# Revit family: Sink-Undermount-Kitchen-KOHLER-Tight-K-33710_1
name_source: partatom
category: Plumbing Fixtures
units: mm (PartAtom-declared; Revit-internal decimal feet)

## family parameters
Cut with Voids When Loaded = No
Host = Face
OmniClass Number = 23.31.13.00
OmniClass Title = Sinks
Part Type = Normal
Room Calculation Point = No
Round Connector Dimension = Use Diameter
Shared = No

## types (6) — shared parameters
ADA Compliant = No
Assembly Code = D2010400
CW Connection = No
Cold Water Inlet = Cold Water Inlet
Date Modified = 08/04/2023
Default Elevation = 36"
Description = Tight Radii Sink 33 Single Bowl
Drain Included = No
HW Connection = No
Height = 9 5/8"
Hot Water Inlet = Hot Water Inlet
Length = 32 1/2"
Manufacturer = Kohler Co.
Master Format 2014 = 22 41 16
Master Format 2014 Name = Residential Lavatories and Sinks
Material = Neoroc
Product Documentation Link = https://www.us.kohler.com
Product Name = Tight
Product Page URL = http://www.us.kohler.com
URL = https://www.us.kohler.com
Vent Connection = No
Waste Connection = Yes
Waste Water Outlet = Waste Water Outlet
WaterSense Certified = No
Width = 18 5/16"

## per-type parameters (varying)
| type | Finish | Model | Type |
| CM1-Matte Black | Kohler-Neoroc-CM1-Matte_Black | K-33710-CM1 | 1 |
| CM2-Matte Brown | Kohler-Neoroc-CM2-Matte_Brown | K-33710-CM2 | 2 |
| CM3-Matte Taupe | Kohler-Neoroc-CM3-Matte_Taupe | K-33710-CM3 | 3 |
| CM4-Matte Grey | Kohler-Neoroc-CM4-Matte_Grey | K-33710-CM4 | 4 |
| CM6-Matte White | KOHLER-Neoroc-CM6-Matte_White | K-33710-CM6 | 5 |
| CM7-Matte Graphite | Kohler-Neoroc-CM7-Matte_Graphite | K-33710-CM7 | 6 |

## geometry (parser evidence)
native form markers: Sweep x5
no freeform markers — native parametric forms only
